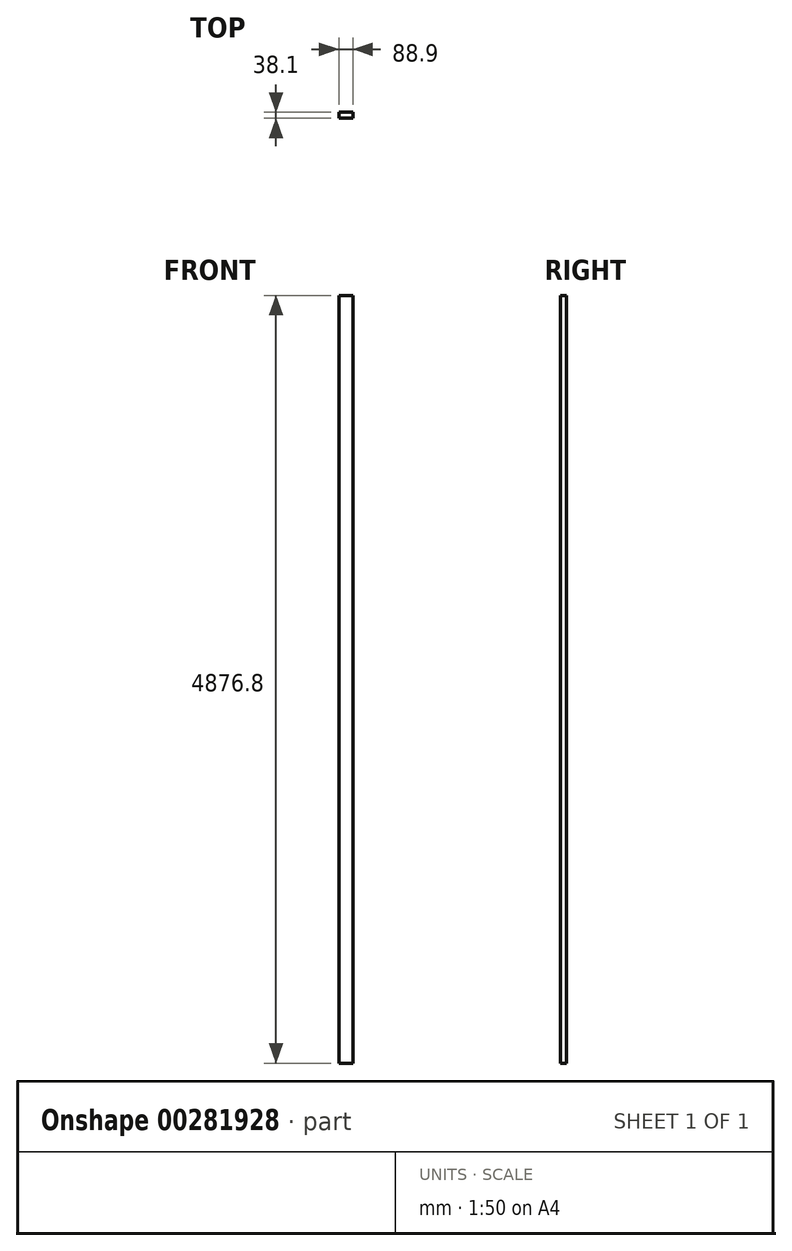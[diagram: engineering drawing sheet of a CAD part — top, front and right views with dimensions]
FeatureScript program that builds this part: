
annotation { "Feature Type Name" : "Feature", "Feature Type Description" : "" }
export const myFeature = defineFeature(function(context is Context, id is Id, definition is map)
    precondition{}
    {
        {
            var Q0;
            Q0=qCreatedBy(makeId("Top.planeOp"),FACE);
            var sketch = newSketch(context, id + "F0", { "sketchPlane" : qUnion([Q0])});
            skLineSegment(sketch, "E0.bottom", {"start": v(44.45, 19.05) * mm, "end": v(-44.45, 19.05) * mm});
            skLineSegment(sketch, "E0.top", {"start": v(44.45, -19.05) * mm, "end": v(-44.45, -19.05) * mm});
            skLineSegment(sketch, "E0.left", {"start": v(44.45, 19.05) * mm, "end": v(44.45, -19.05) * mm});
            skLineSegment(sketch, "E0.right", {"start": v(-44.45, 19.05) * mm, "end": v(-44.45, -19.05) * mm});
            skPoint(sketch, "E0.middle", {"position": v(0, 0) * mm});
            skPoint(sketch, "E1.endSnap0", {"position": v(0, -19.05) * mm});
            skSolve(sketch);
        }
        {
            var Q0;
            Q0=makeQuery(id+"F0.imprint","IMPRINT",FACE,{"disambiguationData":[TD([[makeQuery(id+"F0.imprint","IMPRINT",EDGE,{"derivedFrom":sQuery(id+"F0.wireOp",EDGE,"E0.bottom")}),1.0]])]});
            extrude(context, id + "F1", {"entities" : qUnion([Q0]), "depth" : 4876.8 * mm});
        }
    });
